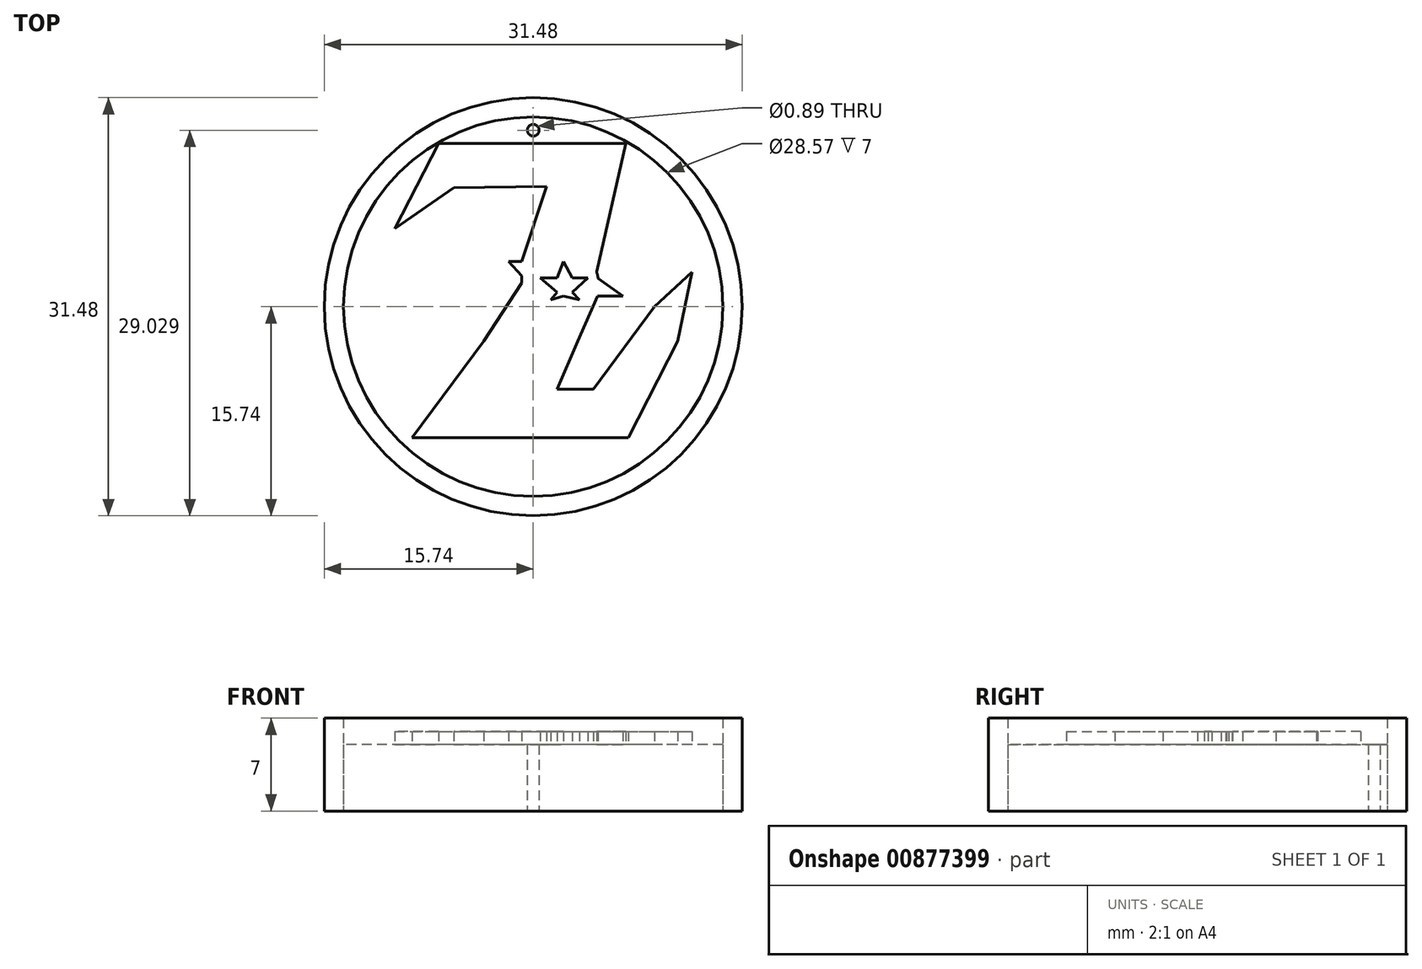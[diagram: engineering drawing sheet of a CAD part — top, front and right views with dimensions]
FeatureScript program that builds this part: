
annotation { "Feature Type Name" : "Feature", "Feature Type Description" : "" }
export const myFeature = defineFeature(function(context is Context, id is Id, definition is map)
    precondition{}
    {
        {
            var Q0;
            Q0=qCreatedBy(makeId("Top.planeOp"),FACE);
            var sketch = newSketch(context, id + "F0", { "sketchPlane" : qUnion([Q0])});
            skCircle(sketch, "E0", {"center": v(0, 0) * mm, "radius": 15.74 * mm});
            skCircle(sketch, "E1", {"center": v(0, 0) * mm, "radius": 14.28 * mm});
            skSolve(sketch);
        }
        {
            var Q0;
            Q0 = qSketchRegion(id + "F0", true);
            extrude(context, id + "F1", {"entities" : qUnion([Q0]), "depth" : 7 * mm, "offsetDistance" : 25 * mm});
        }
        {
            var Q0;
            Q0=makeQuery(id+"F0.imprint","IMPRINT",FACE,{"disambiguationData":[TD([[makeQuery(id+"F0.imprint","IMPRINT",EDGE,{"derivedFrom":sQuery(id+"F0.wireOp",EDGE,"E1")}),1.0]])]});
            extrude(context, id + "F2", {"entities" : qUnion([Q0]), "depth" : 5 * mm, "offsetDistance" : 25 * mm});
        }
        {
            var Q0;
            Q0=qCreatedBy(makeId("Top.planeOp"),FACE);
            var sketch = newSketch(context, id + "F3", { "sketchPlane" : qUnion([Q0])});
            skPoint(sketch, "E2.end.orphan", {"position": v(0, 0) * mm});
            skLineSegment(sketch, "E3", {"start": v(-9.13, -9.87) * mm, "end": v(7.16, -9.87) * mm});
            skLineSegment(sketch, "E4", {"start": v(7.16, -9.87) * mm, "end": v(10.88, -2.6) * mm});
            skLineSegment(sketch, "E5", {"start": v(1.79, -6.23) * mm, "end": v(4.51, -6.23) * mm});
            skLineSegment(sketch, "E6", {"start": v(4.51, -6.23) * mm, "end": v(9.14, 0) * mm});
            skLineSegment(sketch, "E7", {"start": v(10.88, -2.6) * mm, "end": v(11.95, 2.61) * mm});
            skLineSegment(sketch, "E8", {"start": v(9.14, 0) * mm, "end": v(11.95, 2.61) * mm});
            skLineSegment(sketch, "E9", {"start": v(-9.13, -9.87) * mm, "end": v(-3.72, -2.6) * mm});
            skLineSegment(sketch, "E10", {"start": v(1.79, -6.23) * mm, "end": v(3.36, -2.6) * mm});
            skLineSegment(sketch, "E11", {"start": v(3.36, -2.6) * mm, "end": v(4.84, 0.8) * mm});
            skCircle(sketch, "E12", {"center": v(2.28, 1.79) * mm, "radius": 2.63 * mm});
            skLineSegment(sketch, "E13", {"start": v(1.8, 1.09) * mm, "end": v(0.52, 2.17) * mm});
            skLineSegment(sketch, "E14", {"start": v(0.52, 2.17) * mm, "end": v(1.8, 2.17) * mm});
            skLineSegment(sketch, "E15", {"start": v(2.95, 2.17) * mm, "end": v(4.11, 2.17) * mm});
            skLineSegment(sketch, "E16", {"start": v(4.11, 2.17) * mm, "end": v(2.95, 1.09) * mm});
            skLineSegment(sketch, "E17", {"start": v(1.8, 2.17) * mm, "end": v(2.28, 3.4) * mm});
            skLineSegment(sketch, "E18", {"start": v(2.28, 3.4) * mm, "end": v(2.95, 2.17) * mm});
            skLineSegment(sketch, "E19", {"start": v(2.95, 1.09) * mm, "end": v(3.5, 0.5) * mm});
            skLineSegment(sketch, "E20", {"start": v(1.8, 1.09) * mm, "end": v(1.32, 0.5) * mm});
            skLineSegment(sketch, "E21", {"start": v(2.28, 0.8) * mm, "end": v(1.32, 0.5) * mm});
            skLineSegment(sketch, "E22", {"start": v(2.28, 0.8) * mm, "end": v(3.5, 0.5) * mm});
            skLineSegment(sketch, "E23", {"start": v(-0.35, 1.79) * mm, "end": v(-1.85, 3.4) * mm});
            skLineSegment(sketch, "E24", {"start": v(-1.85, 3.4) * mm, "end": v(0, 3.4) * mm});
            skLineSegment(sketch, "E25", {"start": v(4.84, 0.8) * mm, "end": v(6.75, 0.8) * mm});
            skLineSegment(sketch, "E26", {"start": v(6.75, 0.8) * mm, "end": v(4.84, 2.17) * mm});
            skLineSegment(sketch, "E27", {"start": v(5.9, 12.3) * mm, "end": v(-6.34, 12.3) * mm});
            skLineSegment(sketch, "E28", {"start": v(5.9, 12.3) * mm, "end": v(6.99, 12.3) * mm});
            skLineSegment(sketch, "E29", {"start": v(4.87, 2.27) * mm, "end": v(4.84, 2.17) * mm});
            skLineSegment(sketch, "E30", {"start": v(-3.72, -2.6) * mm, "end": v(-0.86, 1.79) * mm});
            skLineSegment(sketch, "E31", {"start": v(-0.86, 1.79) * mm, "end": v(-0.86, 2.34) * mm});
            skLineSegment(sketch, "E32", {"start": v(-6.34, 12.3) * mm, "end": v(-7.14, 12.3) * mm});
            skLineSegment(sketch, "E33", {"start": v(-7.14, 12.3) * mm, "end": v(-10.43, 5.9) * mm});
            skLineSegment(sketch, "E34", {"start": v(-10.43, 5.9) * mm, "end": v(-6, 8.94) * mm});
            skPoint(sketch, "E35.end.orphan", {"position": v(0, 8.94) * mm});
            skLineSegment(sketch, "E36", {"start": v(6.99, 12.3) * mm, "end": v(4.77, 2.64) * mm});
            skLineSegment(sketch, "E37", {"start": v(4.77, 2.64) * mm, "end": v(5.06, 2.78) * mm});
            skLineSegment(sketch, "E38", {"start": v(-0.86, 3.4) * mm, "end": v(1, 9.04) * mm});
            skLineSegment(sketch, "E39", {"start": v(1, 9.04) * mm, "end": v(-6, 8.94) * mm});
            skSolve(sketch);
        }
        {
            var Q0;
            Q0 = qSketchRegion(id + "F3", true);
            extrude(context, id + "F4", {"entities" : qUnion([Q0]), "operationType" : NewBodyOperationType.ADD, "depth" : 6 * mm, "offsetDistance" : 25 * mm});
        }
        {
            var Q0;
            Q0=qCreatedBy(makeId("Top.planeOp"),FACE);
            var sketch = newSketch(context, id + "F5", { "sketchPlane" : qUnion([Q0])});
            skCircle(sketch, "E40", {"center": v(0, 13.29) * mm, "radius": 0.45 * mm});
            skSolve(sketch);
        }
        {
            var Q0;
            Q0 = qSketchRegion(id + "F5", true);
            extrude(context, id + "F6", {"entities" : qUnion([Q0]), "operationType" : NewBodyOperationType.REMOVE, "depth" : 57 * mm, "offsetDistance" : 25 * mm});
        }
    });
